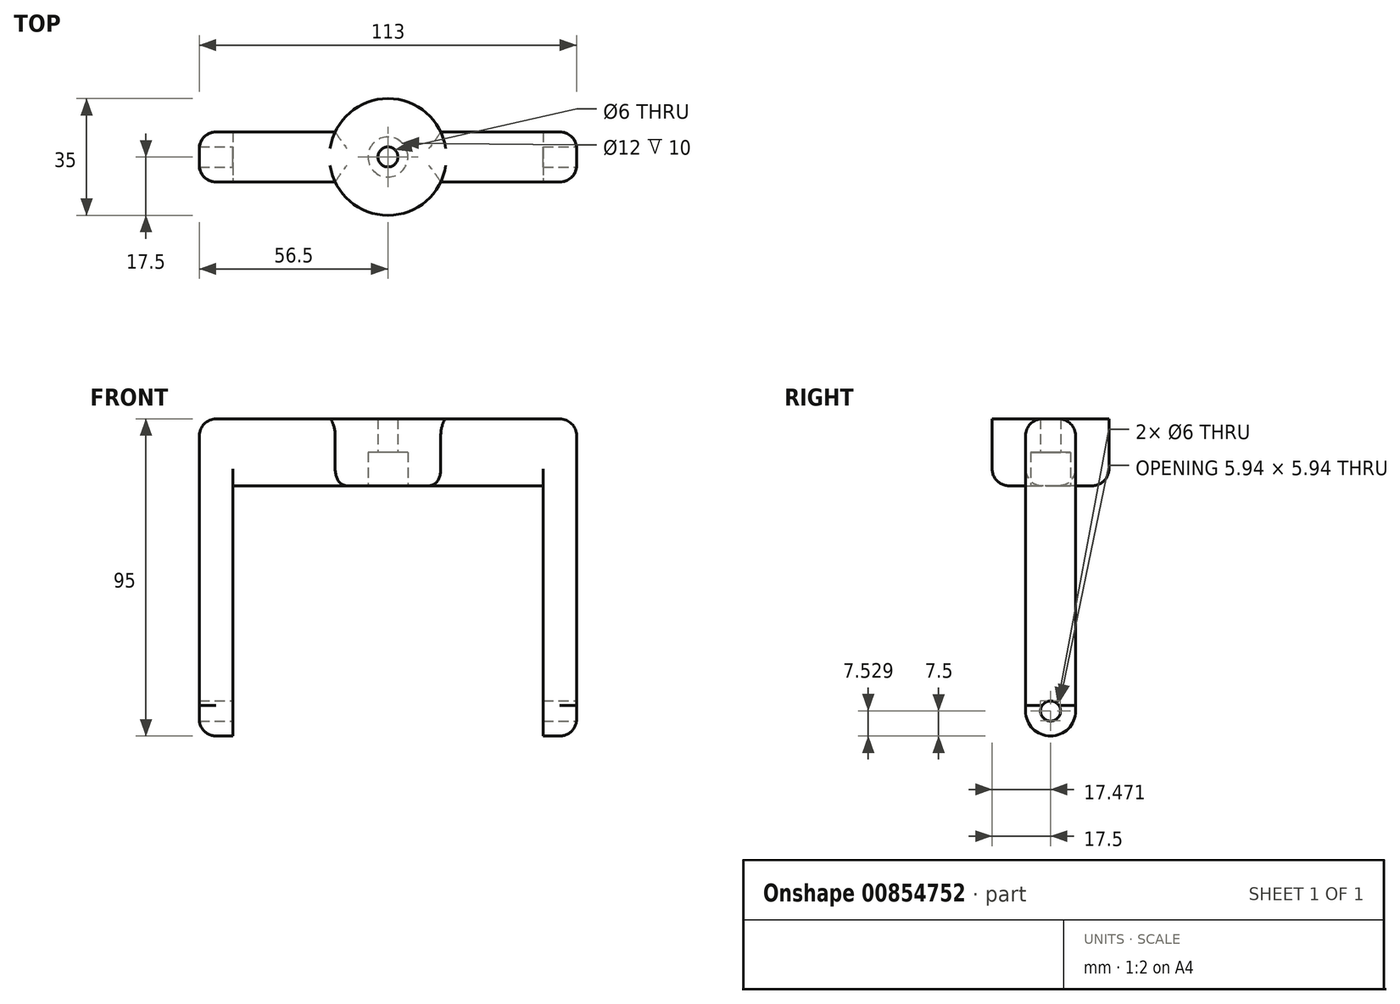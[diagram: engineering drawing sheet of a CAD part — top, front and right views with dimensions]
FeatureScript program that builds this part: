
annotation { "Feature Type Name" : "Feature", "Feature Type Description" : "" }
export const myFeature = defineFeature(function(context is Context, id is Id, definition is map)
    precondition{}
    {
        {
            var Q0;
            Q0=qCreatedBy(makeId("Top.planeOp"),FACE);
            var sketch = newSketch(context, id + "F0", { "sketchPlane" : qUnion([Q0])});
            skCircle(sketch, "E0", {"center": v(0, 0) * mm, "radius": 17.5 * mm});
            skLineSegment(sketch, "E1.bottom", {"start": v(-46.5, 7.5) * mm, "end": v(46.5, 7.5) * mm});
            skLineSegment(sketch, "E1.top", {"start": v(-46.5, -7.5) * mm, "end": v(46.5, -7.5) * mm});
            skLineSegment(sketch, "E1.left", {"start": v(-46.5, 7.5) * mm, "end": v(-46.5, -7.5) * mm});
            skLineSegment(sketch, "E1.right", {"start": v(46.5, 7.5) * mm, "end": v(46.5, -7.5) * mm});
            skLineSegment(sketch, "E2.bottom", {"start": v(-46.5, 7.5) * mm, "end": v(-56.5, 7.5) * mm});
            skLineSegment(sketch, "E2.top", {"start": v(-46.5, -7.5) * mm, "end": v(-56.5, -7.5) * mm});
            skLineSegment(sketch, "E2.right", {"start": v(-56.5, 7.5) * mm, "end": v(-56.5, -7.5) * mm});
            skLineSegment(sketch, "E3.bottom", {"start": v(46.5, 7.5) * mm, "end": v(56.5, 7.5) * mm});
            skLineSegment(sketch, "E3.top", {"start": v(46.5, -7.5) * mm, "end": v(56.5, -7.5) * mm});
            skLineSegment(sketch, "E3.right", {"start": v(56.5, 7.5) * mm, "end": v(56.5, -7.5) * mm});
            skCircle(sketch, "E4", {"center": v(0, 0) * mm, "radius": 6 * mm});
            skCircle(sketch, "E5", {"center": v(0, 0) * mm, "radius": 3 * mm});
            skSolve(sketch);
        }
        {
            var Q0;
            Q0=makeQuery(id+"F0.imprint","IMPRINT",FACE,{"disambiguationData":[TD([[makeQuery(id+"F0.imprint","IMPRINT",EDGE,{"derivedFrom":sQuery(id+"F0.wireOp",EDGE,"E2.bottom")}),1.0]])]});
            var Q1;
            {var subQ5=sQuery(id+"F0.wireOp",EDGE,"E1.left");Q1=makeQuery(id+"F0.imprint","IMPRINT",FACE,{"disambiguationData":[TD([[makeQuery(id+"F0.imprint","IMPRINT",EDGE,{"derivedFrom":subQ5}),1.0]])]});}
            var Q2;
            Q2=makeQuery(id+"F0.imprint","IMPRINT",FACE,{"disambiguationData":[TD([[makeQuery(id+"F0.imprint","IMPRINT",EDGE,{"derivedFrom":sQuery(id+"F0.wireOp",EDGE,"E4")}),-1.0]])]});
            var Q3;
            {var subQ0=sQuery(id+"F0.wireOp",EDGE,"E1.bottom");var subQ1=sQuery(id+"F0.wireOp",EDGE,"E0");var subQ2=makeQuery(id+"F0.imprint","INTERSECT",VERTEX,{"disambiguationData":[OD(0.0)],"derivedFrom":[subQ1,subQ0]});Q3=makeQuery(id+"F0.imprint","IMPRINT",FACE,{"disambiguationData":[TD([[makeQuery(id+"F0.imprint","IMPRINT",EDGE,{"disambiguationData":[TD([[subQ2,1.0]])],"derivedFrom":subQ1}),1.0]])]});}
            var Q4;
            {var subQ0=sQuery(id+"F0.wireOp",EDGE,"E1.top");var subQ1=sQuery(id+"F0.wireOp",EDGE,"E0");var subQ2=makeQuery(id+"F0.imprint","INTERSECT",VERTEX,{"disambiguationData":[OD(0.0)],"derivedFrom":[subQ1,subQ0]});Q4=makeQuery(id+"F0.imprint","IMPRINT",FACE,{"disambiguationData":[TD([[makeQuery(id+"F0.imprint","IMPRINT",EDGE,{"disambiguationData":[TD([[subQ2,-1.0]])],"derivedFrom":subQ1}),1.0]])]});}
            var Q5;
            Q5=makeQuery(id+"F0.imprint","IMPRINT",FACE,{"disambiguationData":[TD([[makeQuery(id+"F0.imprint","IMPRINT",EDGE,{"derivedFrom":sQuery(id+"F0.wireOp",EDGE,"E4")}),1.0]])]});
            var Q6;
            {var subQ5=sQuery(id+"F0.wireOp",EDGE,"E1.right");Q6=makeQuery(id+"F0.imprint","IMPRINT",FACE,{"disambiguationData":[TD([[makeQuery(id+"F0.imprint","IMPRINT",EDGE,{"derivedFrom":subQ5}),-1.0]])]});}
            var Q7;
            Q7=makeQuery(id+"F0.imprint","IMPRINT",FACE,{"disambiguationData":[TD([[makeQuery(id+"F0.imprint","IMPRINT",EDGE,{"derivedFrom":sQuery(id+"F0.wireOp",EDGE,"E3.bottom")}),-1.0]])]});
            extrude(context, id + "F1", {"entities" : qUnion([Q0, Q1, Q2, Q3, Q4, Q5, Q6, Q7]), "depth" : 20 * mm, "offsetDistance" : 25 * mm});
        }
        {
            var Q0;
            Q0=makeQuery(id+"F0.imprint","IMPRINT",FACE,{"disambiguationData":[TD([[makeQuery(id+"F0.imprint","IMPRINT",EDGE,{"derivedFrom":sQuery(id+"F0.wireOp",EDGE,"E2.bottom")}),1.0]])]});
            var Q1;
            Q1=makeQuery(id+"F0.imprint","IMPRINT",FACE,{"disambiguationData":[TD([[makeQuery(id+"F0.imprint","IMPRINT",EDGE,{"derivedFrom":sQuery(id+"F0.wireOp",EDGE,"E3.bottom")}),-1.0]])]});
            extrude(context, id + "F2", {"entities" : qUnion([Q0, Q1]), "operationType" : NewBodyOperationType.ADD, "oppositeDirection" : true, "depth" : 75 * mm, "offsetDistance" : 25 * mm});
        }
        {
            var Q0;
            Q0=makeQuery(id+"F0.imprint","IMPRINT",FACE,{"disambiguationData":[TD([[makeQuery(id+"F0.imprint","IMPRINT",EDGE,{"derivedFrom":sQuery(id+"F0.wireOp",EDGE,"E4")}),1.0]])]});
            extrude(context, id + "F3", {"entities" : qUnion([Q0]), "operationType" : NewBodyOperationType.REMOVE, "depth" : 10 * mm, "offsetDistance" : 25 * mm});
        }
        {
            var Q0;
            {var subQ0=sQuery(id+"F0.wireOp",EDGE,"E3.right");Q0=makeQuery(id+"F2.boolean.opBoolean","MERGE",FACE,{"derivedFrom":[makeQuery(id+"F1.opExtrude","SWEPT_FACE",FACE,{"disambiguationData":[OSD([subQ0])]}),makeQuery(id+"F2.opExtrude","SWEPT_FACE",FACE,{"disambiguationData":[OSD([subQ0])]})]});}
            var sketch = newSketch(context, id + "F4", { "sketchPlane" : qUnion([Q0])});
            skLineSegment(sketch, "E6", {"start": v(7.5, -67.5) * mm, "end": v(-7.5, -67.5) * mm, "construction": true});
            skPoint(sketch, "E7.0", {"position": v(0, -75) * mm});
            skLineSegment(sketch, "E8.0", {"start": v(7.5, 20) * mm, "end": v(7.5, -75) * mm});
            skLineSegment(sketch, "E9.0", {"start": v(-7.5, 20) * mm, "end": v(-7.5, -75) * mm});
            skArc(sketch, "E10", {"start": v(-7.5, -67.5) * mm, "mid": v(0, -75) * mm, "end": v(7.5, -67.5) * mm});
            skCircle(sketch, "E11", {"center": v(0, -67.5) * mm, "radius": 3 * mm});
            skSolve(sketch);
        }
        {
            var Q0;
            {var subQ0=sQuery(id+"F4.wireOp",EDGE,"E8.0");var subQ1=makeQuery(id+"F2.opExtrude","CAP_EDGE",EDGE,{"disambiguationData":[OSD([sQuery(id+"F0.wireOp",EDGE,"E3.right")])],"isStart":false});var subQ2=makeQuery(id+"F4.imprint","INTERSECT",VERTEX,{"derivedFrom":[subQ1,subQ0]});Q0=makeQuery(id+"F4.imprint","IMPRINT",FACE,{"disambiguationData":[TD([[makeQuery(id+"F4.imprint","IMPRINT",EDGE,{"disambiguationData":[TD([[subQ2,1.0]])],"derivedFrom":subQ0}),-1.0]])]});}
            var Q1;
            {var subQ0=sQuery(id+"F4.wireOp",EDGE,"E9.0");var subQ1=makeQuery(id+"F2.opExtrude","CAP_EDGE",EDGE,{"disambiguationData":[OSD([sQuery(id+"F0.wireOp",EDGE,"E3.right")])],"isStart":false});var subQ2=makeQuery(id+"F4.imprint","INTERSECT",VERTEX,{"derivedFrom":[subQ1,subQ0]});Q1=makeQuery(id+"F4.imprint","IMPRINT",FACE,{"disambiguationData":[TD([[makeQuery(id+"F4.imprint","IMPRINT",EDGE,{"disambiguationData":[TD([[subQ2,1.0]])],"derivedFrom":subQ0}),1.0]])]});}
            var Q2;
            Q2=makeQuery(id+"F4.imprint","IMPRINT",FACE,{"disambiguationData":[TD([[makeQuery(id+"F4.imprint","IMPRINT",EDGE,{"derivedFrom":sQuery(id+"F4.wireOp",EDGE,"E11")}),1.0]])]});
            extrude(context, id + "F5", {"entities" : qUnion([Q0, Q1, Q2]), "operationType" : NewBodyOperationType.REMOVE, "endBound" : BoundingType.THROUGH_ALL, "oppositeDirection" : true, "depth" : 25 * mm, "offsetDistance" : 25 * mm});
        }
        {
            var Q0;
            Q0=makeQuery(id+"F1.opExtrude","CAP_EDGE",EDGE,{"disambiguationData":[OSD([sQuery(id+"F0.wireOp",EDGE,"E1.top"),sQuery(id+"F0.wireOp",EDGE,"E2.top")])],"isStart":false});
            var Q1;
            {var subQ0=sQuery(id+"F0.wireOp",EDGE,"E2.right");var subQ1=sQuery(id+"F0.wireOp",EDGE,"E2.top");Q1=makeQuery(id+"F2.boolean.opBoolean","MERGE",EDGE,{"derivedFrom":[makeQuery(id+"F1.opExtrude","SWEPT_EDGE",EDGE,{"disambiguationData":[OSD([subQ1,subQ0])]}),makeQuery(id+"F2.opExtrude","SWEPT_EDGE",EDGE,{"disambiguationData":[OSD([subQ1,subQ0])]})]});}
            var Q2;
            {var subQ0=sQuery(id+"F0.wireOp",EDGE,"E3.right");var subQ1=sQuery(id+"F0.wireOp",EDGE,"E3.top");Q2=makeQuery(id+"F2.boolean.opBoolean","MERGE",EDGE,{"derivedFrom":[makeQuery(id+"F1.opExtrude","SWEPT_EDGE",EDGE,{"disambiguationData":[OSD([subQ1,subQ0])]}),makeQuery(id+"F2.opExtrude","SWEPT_EDGE",EDGE,{"disambiguationData":[OSD([subQ1,subQ0])]})]});}
            var Q3;
            Q3=makeQuery(id+"F1.opExtrude","CAP_EDGE",EDGE,{"disambiguationData":[OSD([sQuery(id+"F0.wireOp",EDGE,"E1.top"),sQuery(id+"F0.wireOp",EDGE,"E3.top")])],"isStart":false});
            var Q4;
            Q4=makeQuery(id+"F1.opExtrude","CAP_EDGE",EDGE,{"disambiguationData":[OSD([sQuery(id+"F0.wireOp",EDGE,"E3.right")])],"isStart":false});
            var Q5;
            Q5=makeQuery(id+"F1.opExtrude","CAP_EDGE",EDGE,{"disambiguationData":[OSD([sQuery(id+"F0.wireOp",EDGE,"E2.right")])],"isStart":false});
            var Q6;
            Q6=makeQuery(id+"F1.opExtrude","CAP_EDGE",EDGE,{"disambiguationData":[OSD([sQuery(id+"F0.wireOp",EDGE,"E1.bottom"),sQuery(id+"F0.wireOp",EDGE,"E2.bottom")])],"isStart":false});
            var Q7;
            Q7=makeQuery(id+"F1.opExtrude","CAP_EDGE",EDGE,{"disambiguationData":[OSD([sQuery(id+"F0.wireOp",EDGE,"E1.bottom"),sQuery(id+"F0.wireOp",EDGE,"E3.bottom")])],"isStart":false});
            var Q8;
            {var subQ0=sQuery(id+"F0.wireOp",EDGE,"E1.top");var subQ1=sQuery(id+"F0.wireOp",EDGE,"E0");Q8=makeQuery(id+"F1.opExtrude","CAP_EDGE",EDGE,{"disambiguationData":[OSD([subQ1]),TDD([makeQuery(id+"F0.imprint","IMPRINT",EDGE,{"disambiguationData":[TD([[makeQuery(id+"F0.imprint","INTERSECT",VERTEX,{"disambiguationData":[OD(0.0)],"derivedFrom":[subQ1,subQ0]}),-1.0]])],"derivedFrom":subQ1})])],"isStart":true});}
            var Q9;
            Q9=makeQuery(id+"F1.opExtrude","CAP_EDGE",EDGE,{"disambiguationData":[OSD([sQuery(id+"F0.wireOp",EDGE,"E1.top"),sQuery(id+"F0.wireOp",EDGE,"E3.top")])],"isStart":true});
            var Q10;
            Q10=makeQuery(id+"F1.opExtrude","CAP_EDGE",EDGE,{"disambiguationData":[OSD([sQuery(id+"F0.wireOp",EDGE,"E1.top"),sQuery(id+"F0.wireOp",EDGE,"E2.top")])],"isStart":true});
            var Q11;
            Q11=makeQuery(id+"F1.opExtrude","CAP_EDGE",EDGE,{"disambiguationData":[OSD([sQuery(id+"F0.wireOp",EDGE,"E1.bottom"),sQuery(id+"F0.wireOp",EDGE,"E2.bottom")])],"isStart":true});
            var Q12;
            Q12=makeQuery(id+"F1.opExtrude","CAP_EDGE",EDGE,{"disambiguationData":[OSD([sQuery(id+"F0.wireOp",EDGE,"E1.bottom"),sQuery(id+"F0.wireOp",EDGE,"E3.bottom")])],"isStart":true});
            var Q13;
            {var subQ0=sQuery(id+"F0.wireOp",EDGE,"E1.bottom");var subQ1=sQuery(id+"F0.wireOp",EDGE,"E0");Q13=makeQuery(id+"F1.opExtrude","CAP_EDGE",EDGE,{"disambiguationData":[OSD([subQ1]),TDD([makeQuery(id+"F0.imprint","IMPRINT",EDGE,{"disambiguationData":[TD([[makeQuery(id+"F0.imprint","INTERSECT",VERTEX,{"disambiguationData":[OD(0.0)],"derivedFrom":[subQ1,subQ0]}),1.0]])],"derivedFrom":subQ1})])],"isStart":true});}
            fillet(context, id + "F6", {"entities" : qUnion([Q0, Q1, Q2, Q3, Q4, Q5, Q6, Q7, Q8, Q9, Q10, Q11, Q12, Q13]), "radius" : 5 * mm, "tangentPropagation" : true, "allowEdgeOverflow" : false});
        }
    });
